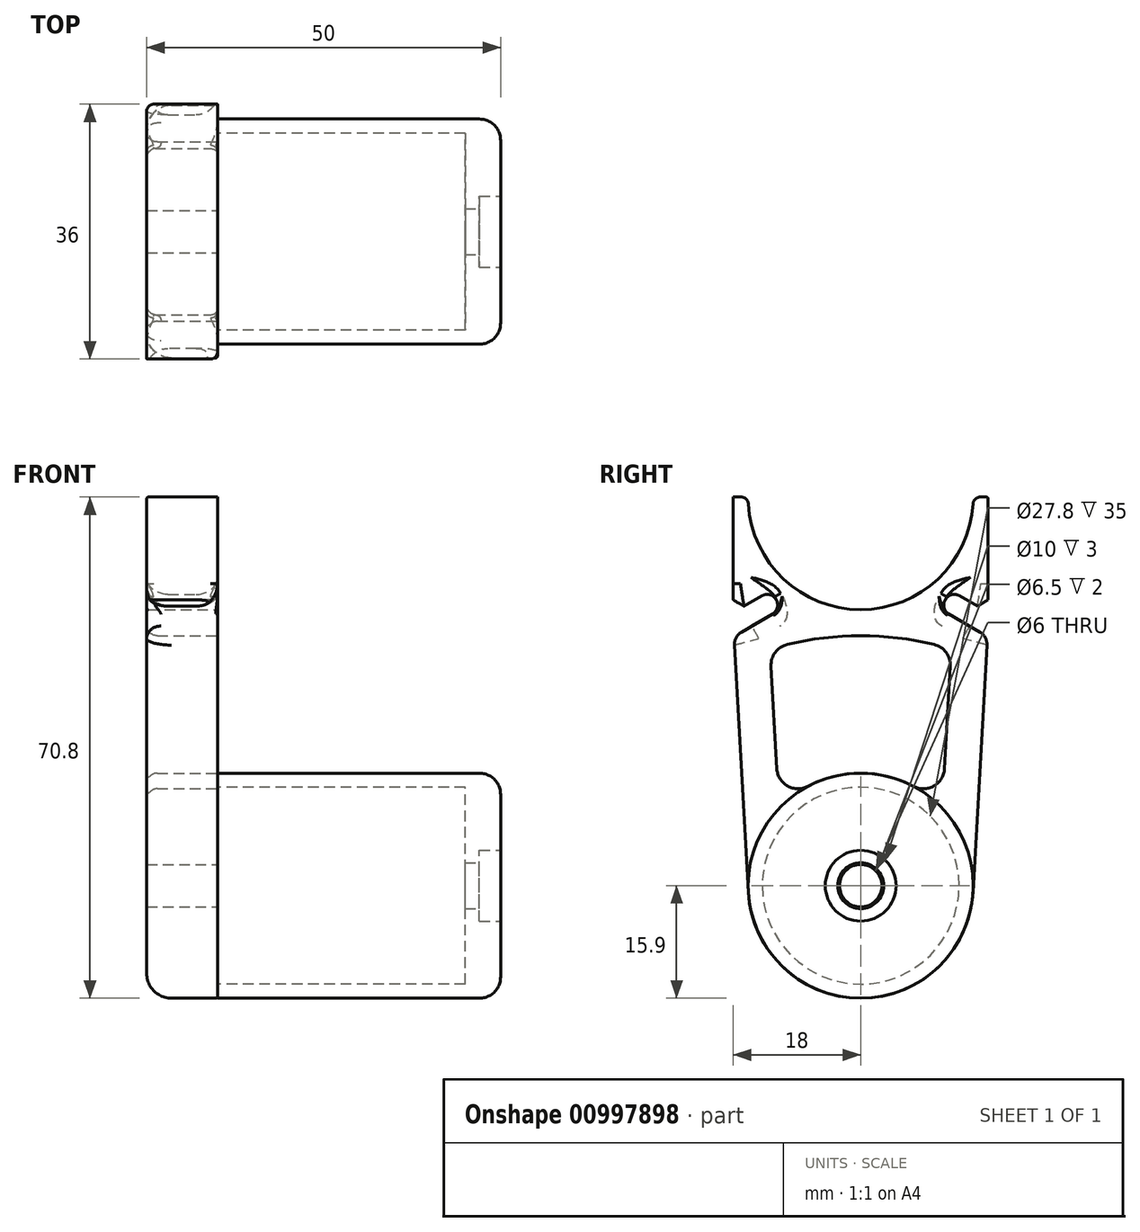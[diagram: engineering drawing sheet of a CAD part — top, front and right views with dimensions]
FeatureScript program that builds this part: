
annotation { "Feature Type Name" : "Feature", "Feature Type Description" : "" }
export const myFeature = defineFeature(function(context is Context, id is Id, definition is map)
    precondition{}
    {
        {
            var Q0;
            Q0=qCreatedBy(makeId("Right.planeOp"),FACE);
            var sketch = newSketch(context, id + "F0", { "sketchPlane" : qUnion([Q0])});
            skArc(sketch, "E0", {"start": v(-15.9, 0) * mm, "mid": v(0, -15.9) * mm, "end": v(15.9, 0) * mm});
            skArc(sketch, "E1", {"start": v(-18, 0) * mm, "mid": v(0, -18) * mm, "end": v(18, 0) * mm, "construction": true});
            skLineSegment(sketch, "E2", {"start": v(0, 0) * mm, "end": v(-18, 0) * mm});
            skLineSegment(sketch, "E3", {"start": v(0, 0) * mm, "end": v(0, -57.9) * mm, "construction": true});
            skCircle(sketch, "E4", {"center": v(0, -54.9) * mm, "radius": 15.9 * mm});
            skLineSegment(sketch, "E5", {"start": v(18, 0) * mm, "end": v(0, 0) * mm});
            skLineSegment(sketch, "E6", {"start": v(-15.93, -54.9) * mm, "end": v(15.93, -54.9) * mm});
            skCircle(sketch, "E7", {"center": v(0, -54.9) * mm, "radius": 3 * mm});
            skPoint(sketch, "E8", {"position": v(0, -18) * mm});
            skPoint(sketch, "E9", {"position": v(0, -39) * mm});
            skCircle(sketch, "E10", {"center": v(0, -54.9) * mm, "radius": 13.9 * mm});
            skLineSegment(sketch, "E11", {"start": v(15.9, 0) * mm, "end": v(15.9, -54.9) * mm, "construction": true});
            skLineSegment(sketch, "E12", {"start": v(-15.9, 0) * mm, "end": v(-15.9, -54.9) * mm, "construction": true});
            skLineSegment(sketch, "E13", {"start": v(18, 0) * mm, "end": v(18, -18) * mm});
            skLineSegment(sketch, "E14", {"start": v(-18, 0) * mm, "end": v(-18, -18) * mm});
            skLineSegment(sketch, "E15", {"start": v(18, -18) * mm, "end": v(15.87, -55.8) * mm});
            skLineSegment(sketch, "E16", {"start": v(-18, -18) * mm, "end": v(-15.87, -55.8) * mm});
            skLineSegment(sketch, "E17", {"start": v(-18, -18) * mm, "end": v(-11.94, -14.5) * mm, "construction": true});
            skCircle(sketch, "E18", {"center": v(-11.94, -14.5) * mm, "radius": 1.5 * mm});
            skLineSegment(sketch, "E19", {"start": v(-11.94, -14.5) * mm, "end": v(-12.69, -13.2) * mm, "construction": true});
            skLineSegment(sketch, "E20", {"start": v(-12.69, -13.2) * mm, "end": v(-18, -16.27) * mm});
            skLineSegment(sketch, "E21", {"start": v(-11.94, -14.5) * mm, "end": v(-11.19, -15.8) * mm, "construction": true});
            skLineSegment(sketch, "E22", {"start": v(-11.19, -15.8) * mm, "end": v(-17.9, -19.68) * mm});
            skLineSegment(sketch, "E23.MirrorCS", {"start": v(12.69, -13.2) * mm, "end": v(18, -16.27) * mm});
            skCircle(sketch, "E24.MirrorC", {"center": v(11.94, -14.5) * mm, "radius": 1.5 * mm});
            skLineSegment(sketch, "E25.MirrorCS", {"start": v(11.19, -15.8) * mm, "end": v(17.9, -19.68) * mm});
            skLineSegment(sketch, "E26", {"start": v(-12.8, -21.48) * mm, "end": v(-11.53, -43.95) * mm});
            skLineSegment(sketch, "E27", {"start": v(12.8, -21.48) * mm, "end": v(11.53, -43.95) * mm});
            skArc(sketch, "E28.trimOffspring", {"start": v(-12.8, -21.48) * mm, "mid": v(0, -25.18) * mm, "end": v(12.8, -21.48) * mm});
            skLineSegment(sketch, "E29", {"start": v(12.8, -21.48) * mm, "end": v(-12.8, -21.48) * mm, "construction": true});
            skArc(sketch, "E30", {"start": v(12.8, -21.48) * mm, "mid": v(0, -19.59) * mm, "end": v(-12.8, -21.48) * mm});
            skLineSegment(sketch, "E31", {"start": v(-17.9, -19.68) * mm, "end": v(17.9, -19.68) * mm});
            skLineSegment(sketch, "E32", {"start": v(12.69, -13.2) * mm, "end": v(11.19, -15.8) * mm});
            skLineSegment(sketch, "E33", {"start": v(-12.69, -13.2) * mm, "end": v(-11.19, -15.8) * mm});
            skSolve(sketch);
        }
        {
            var Q0;
            {var subQ0=sQuery(id+"F0.wireOp",EDGE,"hCOq8FCj-mZPl-xb8t-M9cf-22ctuRcThsnU");Q0=makeQuery(id+"F0.imprint","IMPRINT",FACE,{"disambiguationData":[TD([[makeQuery(id+"F0.imprint","IMPRINT",EDGE,{"derivedFrom":subQ0}),-1.0]])]});}
            var Q1;
            {var subQ0=sQuery(id+"F0.wireOp",EDGE,"TaPYkj7w-x2AP-gBk1-BHdD-hzMeUHBt6qgc");Q1=makeQuery(id+"F0.imprint","IMPRINT",FACE,{"disambiguationData":[TD([[makeQuery(id+"F0.imprint","IMPRINT",EDGE,{"derivedFrom":subQ0}),1.0]])]});}
            var Q2;
            {var subQ5=sQuery(id+"F0.wireOp",EDGE,"6MMxsrJf-m4Ve-tTBv-1n6J-gzjikBUi8nmd");Q2=makeQuery(id+"F0.imprint","IMPRINT",FACE,{"disambiguationData":[TD([[makeQuery(id+"F0.imprint","IMPRINT",EDGE,{"derivedFrom":subQ5}),-1.0]])]});}
            var Q3;
            {var subQ0=sQuery(id+"F0.wireOp",EDGE,"ev4YOO8p-w140-sNIP-OVyz-yG1uIH5KCiYH");Q3=makeQuery(id+"F0.imprint","IMPRINT",FACE,{"disambiguationData":[TD([[makeQuery(id+"F0.imprint","IMPRINT",EDGE,{"derivedFrom":subQ0}),1.0]])]});}
            var Q4;
            {var subQ0=sQuery(id+"F0.wireOp",EDGE,"TuPFUTSs-Mdkt-fsBn-U9RT-kbwSlqQY4cYo");Q4=makeQuery(id+"F0.imprint","IMPRINT",FACE,{"disambiguationData":[TD([[makeQuery(id+"F0.imprint","IMPRINT",EDGE,{"derivedFrom":subQ0}),-1.0]])]});}
            var Q5;
            {var subQ0=sQuery(id+"F0.wireOp",EDGE,"BNH5TMII-rD8g-z0Vy-wBGW-XPU128KKju92");Q5=makeQuery(id+"F0.imprint","IMPRINT",FACE,{"disambiguationData":[TD([[makeQuery(id+"F0.imprint","IMPRINT",EDGE,{"derivedFrom":subQ0}),-1.0]])]});}
            var Q6;
            Q6=makeQuery(id+"F0.imprint","IMPRINT",FACE,{"disambiguationData":[TD([[makeQuery(id+"F0.imprint","IMPRINT",EDGE,{"derivedFrom":sQuery(id+"F0.wireOp",EDGE,"TuPFUTSs-Mdkt-fsBn-U9RT-kbwSlqQY4cYo")}),1.0]])]});
            var Q7;
            {var subQ0=sQuery(id+"F0.wireOp",EDGE,"qgnF70fx-FksF-CE6E-BVKT-dnHn9iPgRWFa");Q7=makeQuery(id+"F0.imprint","IMPRINT",FACE,{"disambiguationData":[TD([[makeQuery(id+"F0.imprint","IMPRINT",EDGE,{"derivedFrom":subQ0}),1.0]])]});}
            var Q8;
            {var subQ1=sQuery(id+"F0.wireOp",EDGE,"E0");var subQ3=sQuery(id+"F0.wireOp",EDGE,"8emj3K5Y-vfSL-qXS8-FGDl-GD4WZCmneeYx");var subQ4=makeQuery(id+"F0.imprint","INTERSECT",VERTEX,{"derivedFrom":[subQ1,subQ3]});Q8=makeQuery(id+"F0.imprint","IMPRINT",FACE,{"disambiguationData":[TD([[makeQuery(id+"F0.imprint","IMPRINT",EDGE,{"disambiguationData":[TD([[subQ4,1.0]])],"derivedFrom":subQ3}),1.0]])]});}
            var Q9;
            {var subQ4=sQuery(id+"F0.wireOp",EDGE,"4b9Ultii-NDLb-Hdy1-wgni-m4wKdF3KNtY6");Q9=makeQuery(id+"F0.imprint","IMPRINT",FACE,{"disambiguationData":[TD([[makeQuery(id+"F0.imprint","IMPRINT",EDGE,{"derivedFrom":subQ4}),1.0]])]});}
            var Q10;
            {var subQ1=sQuery(id+"F0.wireOp",EDGE,"E0");var subQ3=sQuery(id+"F0.wireOp",EDGE,"9gYWYnP8-HUed-MIOg-rzxO-PlR66y88BDPI");var subQ4=makeQuery(id+"F0.imprint","INTERSECT",VERTEX,{"derivedFrom":[subQ1,subQ3]});Q10=makeQuery(id+"F0.imprint","IMPRINT",FACE,{"disambiguationData":[TD([[makeQuery(id+"F0.imprint","IMPRINT",EDGE,{"disambiguationData":[TD([[subQ4,1.0]])],"derivedFrom":subQ3}),-1.0]])]});}
            var Q11;
            {var subQ0=sQuery(id+"F0.wireOp",EDGE,"E12");var subQ1=sQuery(id+"F0.wireOp",EDGE,"E1");var subQ2=makeQuery(id+"F0.imprint","INTERSECT",VERTEX,{"derivedFrom":[subQ1,subQ0]});Q11=makeQuery(id+"F0.imprint","IMPRINT",FACE,{"disambiguationData":[TD([[makeQuery(id+"F0.imprint","IMPRINT",EDGE,{"disambiguationData":[TD([[subQ2,-1.0]])],"derivedFrom":subQ1}),-1.0]])]});}
            var Q12;
            {var subQ1=sQuery(id+"F0.wireOp",EDGE,"8emj3K5Y-vfSL-qXS8-FGDl-GD4WZCmneeYx");var subQ3=sQuery(id+"F0.wireOp",EDGE,"E1");var subQ4=makeQuery(id+"F0.imprint","INTERSECT",VERTEX,{"derivedFrom":[subQ3,subQ1]});Q12=makeQuery(id+"F0.imprint","IMPRINT",FACE,{"disambiguationData":[TD([[makeQuery(id+"F0.imprint","IMPRINT",EDGE,{"disambiguationData":[TD([[subQ4,-1.0]])],"derivedFrom":subQ3}),-1.0]])]});}
            var Q13;
            {var subQ0=sQuery(id+"F0.wireOp",EDGE,"9gYWYnP8-HUed-MIOg-rzxO-PlR66y88BDPI");var subQ1=sQuery(id+"F0.wireOp",EDGE,"E1");var subQ2=makeQuery(id+"F0.imprint","INTERSECT",VERTEX,{"derivedFrom":[subQ1,subQ0]});Q13=makeQuery(id+"F0.imprint","IMPRINT",FACE,{"disambiguationData":[TD([[makeQuery(id+"F0.imprint","IMPRINT",EDGE,{"disambiguationData":[TD([[subQ2,-1.0]])],"derivedFrom":subQ1}),-1.0]])]});}
            var Q14;
            Q14=makeQuery(id+"F0.imprint","IMPRINT",FACE,{"disambiguationData":[TD([[makeQuery(id+"F0.imprint","IMPRINT",EDGE,{"derivedFrom":sQuery(id+"F0.wireOp",EDGE,"6R3bmdMW-g6tU-yjxk-HsSZ-tdWfC2ykRPMh")}),-1.0]])]});
            var Q15;
            {var subQ0=sQuery(id+"F0.wireOp",EDGE,"E4");var subQ7=makeQuery(id+"F0.imprint","INTERSECT",VERTEX,{"derivedFrom":[subQ0,sQuery(id+"F0.wireOp",EDGE,"E16")]});Q15=makeQuery(id+"F0.imprint","IMPRINT",FACE,{"disambiguationData":[TD([[makeQuery(id+"F0.imprint","IMPRINT",EDGE,{"disambiguationData":[TD([[subQ7,1.0]])],"derivedFrom":subQ0}),1.0]])]});}
            var Q16;
            {var subQ8=sQuery(id+"F0.wireOp",EDGE,"E26");Q16=makeQuery(id+"F0.imprint","IMPRINT",FACE,{"disambiguationData":[TD([[makeQuery(id+"F0.imprint","IMPRINT",EDGE,{"derivedFrom":subQ8}),-1.0]])]});}
            var Q17;
            {var subQ1=sQuery(id+"F0.wireOp",EDGE,"E4");var subQ6=makeQuery(id+"F0.imprint","INTERSECT",VERTEX,{"derivedFrom":[subQ1,sQuery(id+"F0.wireOp",EDGE,"E27")]});Q17=makeQuery(id+"F0.imprint","IMPRINT",FACE,{"disambiguationData":[TD([[makeQuery(id+"F0.imprint","IMPRINT",EDGE,{"disambiguationData":[TD([[subQ6,1.0]])],"derivedFrom":subQ1}),1.0]])]});}
            var Q18;
            Q18=makeQuery(id+"F0.imprint","IMPRINT",FACE,{"disambiguationData":[TD([[makeQuery(id+"F0.imprint","IMPRINT",EDGE,{"derivedFrom":sQuery(id+"F0.wireOp",EDGE,"SB0yHOxI-lRpt-iEP2-3W7u-v9B3a5rHVDpD")}),-1.0]])]});
            var Q19;
            {var subQ4=sQuery(id+"F0.wireOp",EDGE,"E22");Q19=makeQuery(id+"F0.imprint","IMPRINT",FACE,{"disambiguationData":[TD([[makeQuery(id+"F0.imprint","IMPRINT",EDGE,{"derivedFrom":subQ4}),1.0]])]});}
            var Q20;
            {var subQ0=sQuery(id+"F0.wireOp",EDGE,"E16");var subQ1=sQuery(id+"F0.wireOp",EDGE,"E4");var subQ2=makeQuery(id+"F0.imprint","INTERSECT",VERTEX,{"derivedFrom":[subQ1,subQ0]});Q20=makeQuery(id+"F0.imprint","IMPRINT",FACE,{"disambiguationData":[TD([[makeQuery(id+"F0.imprint","IMPRINT",EDGE,{"disambiguationData":[TD([[subQ2,1.0]])],"derivedFrom":subQ1}),-1.0]])]});}
            var Q21;
            {var subQ0=sQuery(id+"F0.wireOp",EDGE,"E15");var subQ1=sQuery(id+"F0.wireOp",EDGE,"E4");var subQ2=makeQuery(id+"F0.imprint","INTERSECT",VERTEX,{"derivedFrom":[subQ1,subQ0]});Q21=makeQuery(id+"F0.imprint","IMPRINT",FACE,{"disambiguationData":[TD([[makeQuery(id+"F0.imprint","IMPRINT",EDGE,{"disambiguationData":[TD([[subQ2,-1.0]])],"derivedFrom":subQ1}),-1.0]])]});}
            var Q22;
            {var subQ0=sQuery(id+"F0.wireOp",EDGE,"E33");Q22=makeQuery(id+"F0.imprint","IMPRINT",FACE,{"disambiguationData":[TD([[makeQuery(id+"F0.imprint","IMPRINT",EDGE,{"derivedFrom":subQ0}),1.0]])]});}
            var Q23;
            {var subQ0=sQuery(id+"F0.wireOp",EDGE,"E32");Q23=makeQuery(id+"F0.imprint","IMPRINT",FACE,{"disambiguationData":[TD([[makeQuery(id+"F0.imprint","IMPRINT",EDGE,{"derivedFrom":subQ0}),-1.0]])]});}
            var Q24;
            {var subQ5=sQuery(id+"F0.wireOp",EDGE,"E27");Q24=makeQuery(id+"F0.imprint","IMPRINT",FACE,{"disambiguationData":[TD([[makeQuery(id+"F0.imprint","IMPRINT",EDGE,{"derivedFrom":subQ5}),1.0]])]});}
            var Q25;
            {var subQ0=sQuery(id+"F0.wireOp",EDGE,"E10");var subQ1=sQuery(id+"F0.wireOp",EDGE,"E6");var subQ2=makeQuery(id+"F0.imprint","INTERSECT",VERTEX,{"disambiguationData":[OD(0.0)],"derivedFrom":[subQ1,subQ0]});Q25=makeQuery(id+"F0.imprint","IMPRINT",FACE,{"disambiguationData":[TD([[makeQuery(id+"F0.imprint","IMPRINT",EDGE,{"disambiguationData":[TD([[subQ2,-1.0]])],"derivedFrom":subQ1}),-1.0]])]});}
            var Q26;
            {var subQ0=sQuery(id+"F0.wireOp",EDGE,"E10");var subQ1=sQuery(id+"F0.wireOp",EDGE,"E6");var subQ2=makeQuery(id+"F0.imprint","INTERSECT",VERTEX,{"disambiguationData":[OD(0.0)],"derivedFrom":[subQ1,subQ0]});Q26=makeQuery(id+"F0.imprint","IMPRINT",FACE,{"disambiguationData":[TD([[makeQuery(id+"F0.imprint","IMPRINT",EDGE,{"disambiguationData":[TD([[subQ2,-1.0]])],"derivedFrom":subQ1}),1.0]])]});}
            extrude(context, id + "F1", {"entities" : qUnion([Q0, Q1, Q2, Q3, Q4, Q5, Q6, Q7, Q8, Q9, Q10, Q11, Q12, Q13, Q14, Q15, Q16, Q17, Q18, Q19, Q20, Q21, Q22, Q23, Q24, Q25, Q26]), "endBound" : BoundingType.SYMMETRIC, "oppositeDirection" : true, "depth" : 10 * mm, "offsetDistance" : 25 * mm, "hasSecondDirection" : true, "secondDirectionOppositeDirection" : false, "secondDirectionDepth" : 3 * mm});
        }
        {
            var Q0;
            Q0=makeQuery(id+"F1.opExtrude","SWEPT_EDGE",EDGE,{"disambiguationData":[OSD([sQuery(id+"F0.wireOp",EDGE,"E14"),sQuery(id+"F0.wireOp",EDGE,"E20")])]});
            var Q1;
            Q1=makeQuery(id+"F1.opExtrude","SWEPT_EDGE",EDGE,{"disambiguationData":[OSD([sQuery(id+"F0.wireOp",EDGE,"E13"),sQuery(id+"F0.wireOp",EDGE,"E23.MirrorCS")])]});
            chamfer(context, id + "F2", {"entities" : qUnion([Q0, Q1]), "width" : 1 * mm, "tangentPropagation" : true});
        }
        {
            var Q0;
            Q0=makeQuery(id+"F1.opExtrude","CAP_EDGE",EDGE,{"disambiguationData":[OSD([sQuery(id+"F0.wireOp",EDGE,"E20")])],"isStart":true});
            var Q1;
            Q1=makeQuery(id+"F1.opExtrude","CAP_EDGE",EDGE,{"disambiguationData":[OSD([sQuery(id+"F0.wireOp",EDGE,"E20")])],"isStart":false});
            var Q2;
            Q2=makeQuery(id+"F1.opExtrude","CAP_EDGE",EDGE,{"disambiguationData":[OSD([sQuery(id+"F0.wireOp",EDGE,"E23.MirrorCS")])],"isStart":false});
            var Q3;
            Q3=makeQuery(id+"F1.opExtrude","CAP_EDGE",EDGE,{"disambiguationData":[OSD([sQuery(id+"F0.wireOp",EDGE,"E23.MirrorCS")])],"isStart":true});
            fillet(context, id + "F3", {"entities" : qUnion([Q0, Q1, Q2, Q3]), "tangentPropagation" : true, "radius" : 3 * mm, "defaultsChanged" : false, "vertexSettings" : [], "allowEdgeOverflow" : false});
        }
        {
            var Q0;
            Q0=makeQuery(id+"F3.opFillet","BLEND_EDGE",EDGE,{"blendedFrom":[makeQuery(id+"F1.opExtrude","CAP_EDGE",EDGE,{"disambiguationData":[OSD([sQuery(id+"F0.wireOp",EDGE,"E20")])],"isStart":true}),makeQuery(id+"F1.opExtrude","SWEPT_FACE",FACE,{"disambiguationData":[OSD([sQuery(id+"F0.wireOp",EDGE,"E14")])]})],"blendedInto":[makeQuery(id+"F1.opExtrude","SWEPT_FACE",FACE,{"disambiguationData":[OSD([sQuery(id+"F0.wireOp",EDGE,"E14")])]})]});
            var Q1;
            Q1=makeQuery(id+"F1.opExtrude","CAP_EDGE",EDGE,{"disambiguationData":[OSD([sQuery(id+"F0.wireOp",EDGE,"E13")])],"isStart":false});
            fillet(context, id + "F4", {"entities" : qUnion([Q0, Q1]), "tangentPropagation" : true, "radius" : 1 * mm, "defaultsChanged" : false, "vertexSettings" : [], "allowEdgeOverflow" : false});
        }
        {
            var Q0;
            Q0=makeQuery(id+"F1.opExtrude","SWEPT_EDGE",EDGE,{"disambiguationData":[OSD([sQuery(id+"F0.wireOp",EDGE,"E0"),sQuery(id+"F0.wireOp",EDGE,"E2")])]});
            var Q1;
            Q1=makeQuery(id+"F1.opExtrude","SWEPT_EDGE",EDGE,{"disambiguationData":[OSD([sQuery(id+"F0.wireOp",EDGE,"E0"),sQuery(id+"F0.wireOp",EDGE,"E5")])]});
            fillet(context, id + "F5", {"entities" : qUnion([Q0, Q1]), "tangentPropagation" : true, "radius" : 1 * mm, "defaultsChanged" : true, "vertexSettings" : [], "allowEdgeOverflow" : false});
        }
        {
            var Q0;
            Q0=makeQuery(id+"F1.opExtrude","CAP_EDGE",EDGE,{"disambiguationData":[OSD([sQuery(id+"F0.wireOp",EDGE,"E0")])],"isStart":false});
            fillet(context, id + "F6", {"entities" : qUnion([Q0]), "tangentPropagation" : true, "radius" : .25 * mm, "defaultsChanged" : false, "vertexSettings" : [], "allowEdgeOverflow" : false});
        }
        {
            var Q0;
            Q0=makeQuery(id+"F1.opExtrude","CAP_EDGE",EDGE,{"disambiguationData":[OSD([sQuery(id+"F0.wireOp",EDGE,"E15")])],"isStart":false});
            fillet(context, id + "F7", {"entities" : qUnion([Q0]), "tangentPropagation" : true, "radius" : 3.5 * mm, "defaultsChanged" : false, "vertexSettings" : [], "allowEdgeOverflow" : false});
        }
        {
            var Q0;
            Q0=makeQuery(id+"F1.opExtrude","SWEPT_EDGE",EDGE,{"disambiguationData":[OSD([sQuery(id+"F0.wireOp",EDGE,"E23.MirrorCS"),sQuery(id+"F0.wireOp",EDGE,"E24.MirrorC"),sQuery(id+"F0.wireOp",EDGE,"E32")])]});
            var Q1;
            Q1=makeQuery(id+"F3.opFillet","BLEND_EDGE",EDGE,{"blendedFrom":[makeQuery(id+"F1.opExtrude","CAP_EDGE",EDGE,{"disambiguationData":[OSD([sQuery(id+"F0.wireOp",EDGE,"E20")])],"isStart":false}),makeQuery(id+"F1.opExtrude","SWEPT_FACE",FACE,{"disambiguationData":[OSD([sQuery(id+"F0.wireOp",EDGE,"E33")])]})],"blendedInto":[makeQuery(id+"F1.opExtrude","SWEPT_FACE",FACE,{"disambiguationData":[OSD([sQuery(id+"F0.wireOp",EDGE,"E33")])]})]});
            fillet(context, id + "F8", {"entities" : qUnion([Q0, Q1]), "tangentPropagation" : true, "radius" : 1.5 * mm, "defaultsChanged" : true, "vertexSettings" : [], "allowEdgeOverflow" : false});
        }
        {
            var Q0;
            Q0=makeQuery(id+"F1.opExtrude","CAP_EDGE",EDGE,{"disambiguationData":[OSD([sQuery(id+"F0.wireOp",EDGE,"E32")])],"isStart":false});
            var Q1;
            Q1=makeQuery(id+"F1.opExtrude","CAP_EDGE",EDGE,{"disambiguationData":[OSD([sQuery(id+"F0.wireOp",EDGE,"E32")])],"isStart":true});
            var Q2;
            Q2=makeQuery(id+"F1.opExtrude","CAP_EDGE",EDGE,{"disambiguationData":[OSD([sQuery(id+"F0.wireOp",EDGE,"E33")])],"isStart":false});
            var Q3;
            Q3=makeQuery(id+"F1.opExtrude","CAP_EDGE",EDGE,{"disambiguationData":[OSD([sQuery(id+"F0.wireOp",EDGE,"E33")])],"isStart":true});
            fillet(context, id + "F9", {"entities" : qUnion([Q0, Q1, Q2, Q3]), "tangentPropagation" : true, "radius" : 1 * mm, "defaultsChanged" : false, "vertexSettings" : [], "allowEdgeOverflow" : false});
        }
        {
            var Q0;
            Q0=makeQuery(id+"F1.opExtrude","SWEPT_EDGE",EDGE,{"disambiguationData":[OSD([sQuery(id+"F0.wireOp",EDGE,"E24.MirrorC"),sQuery(id+"F0.wireOp",EDGE,"E25.MirrorCS"),sQuery(id+"F0.wireOp",EDGE,"E32")])]});
            var Q1;
            {var subQ0=sQuery(id+"F0.wireOp",EDGE,"E2");var subQ1=sQuery(id+"F0.wireOp",EDGE,"E0");var subQ2=makeQuery(id+"F1.opExtrude","CAP_FACE",FACE,{"disambiguationData":[OSD([subQ1,subQ0,sQuery(id+"F0.wireOp",EDGE,"E4"),sQuery(id+"F0.wireOp",EDGE,"E5"),sQuery(id+"F0.wireOp",EDGE,"E7"),sQuery(id+"F0.wireOp",EDGE,"SB0yHOxI-lRpt-iEP2-3W7u-v9B3a5rHVDpD"),sQuery(id+"F0.wireOp",EDGE,"LhZdfopr-r1uI-wH8t-D8PB-L3U7t8i66CS0"),sQuery(id+"F0.wireOp",EDGE,"cogAvgOB-P8PS-PaiP-QbT0-jrrfWqRzv5wB"),sQuery(id+"F0.wireOp",EDGE,"6R3bmdMW-g6tU-yjxk-HsSZ-tdWfC2ykRPMh"),sQuery(id+"F0.wireOp",EDGE,"E13"),sQuery(id+"F0.wireOp",EDGE,"E14"),sQuery(id+"F0.wireOp",EDGE,"E15"),sQuery(id+"F0.wireOp",EDGE,"E16"),sQuery(id+"F0.wireOp",EDGE,"E20"),sQuery(id+"F0.wireOp",EDGE,"E22"),sQuery(id+"F0.wireOp",EDGE,"E23.MirrorCS"),sQuery(id+"F0.wireOp",EDGE,"E25.MirrorCS"),sQuery(id+"F0.wireOp",EDGE,"E26"),sQuery(id+"F0.wireOp",EDGE,"E27"),sQuery(id+"F0.wireOp",EDGE,"E30"),sQuery(id+"F0.wireOp",EDGE,"E32"),sQuery(id+"F0.wireOp",EDGE,"E33")])],"isStart":false});Q1=makeQuery(id+"F6.opFillet","BLEND_EDGE",EDGE,{"blendedFrom":[makeQuery(id+"F5.opFillet","BLEND_EDGE",EDGE,{"blendedFrom":[makeQuery(id+"F1.opExtrude","SWEPT_EDGE",EDGE,{"disambiguationData":[OSD([subQ1,subQ0])]}),subQ2],"blendedInto":[subQ2]}),subQ2],"blendedInto":[subQ2]});}
            var Q2;
            {var subQ0=sQuery(id+"F0.wireOp",EDGE,"E2");Q2=makeQuery(id+"F6.opFillet","BLEND_EDGE",EDGE,{"blendedFrom":[makeQuery(id+"F4.opFillet","BLEND_EDGE",EDGE,{"disambiguationData":[OD(1.0)],"blendedFrom":[makeQuery(id+"F1.opExtrude","CAP_EDGE",EDGE,{"disambiguationData":[OSD([sQuery(id+"F0.wireOp",EDGE,"E14")])],"isStart":true}),makeQuery(id+"F1.opExtrude","SWEPT_FACE",FACE,{"disambiguationData":[OSD([subQ0])]})],"blendedInto":[makeQuery(id+"F1.opExtrude","SWEPT_FACE",FACE,{"disambiguationData":[OSD([subQ0])]})]}),makeQuery(id+"F1.opExtrude","CAP_EDGE",EDGE,{"disambiguationData":[OSD([subQ0])],"isStart":false})],"blendedInto":[]});}
            var Q3;
            {var subQ0=sQuery(id+"F0.wireOp",EDGE,"E14");Q3=makeQuery(id+"F6.opFillet","BLEND_EDGE",EDGE,{"blendedFrom":[makeQuery(id+"F4.opFillet","BLEND_EDGE",EDGE,{"disambiguationData":[OD(1.0)],"blendedFrom":[makeQuery(id+"F1.opExtrude","CAP_EDGE",EDGE,{"disambiguationData":[OSD([subQ0])],"isStart":true}),makeQuery(id+"F1.opExtrude","SWEPT_FACE",FACE,{"disambiguationData":[OSD([sQuery(id+"F0.wireOp",EDGE,"E2")])]})],"blendedInto":[makeQuery(id+"F1.opExtrude","SWEPT_FACE",FACE,{"disambiguationData":[OSD([sQuery(id+"F0.wireOp",EDGE,"E2")])]})]}),makeQuery(id+"F4.opFillet","BLEND_FACE",FACE,{"disambiguationData":[OSD([subQ0]),OD(1.0)]})],"blendedInto":[makeQuery(id+"F4.opFillet","BLEND_FACE",FACE,{"disambiguationData":[OSD([subQ0]),OD(1.0)]})]});}
            var Q4;
            {var subQ0=sQuery(id+"F0.wireOp",EDGE,"E2");var subQ1=sQuery(id+"F0.wireOp",EDGE,"E0");Q4=makeQuery(id+"F6.opFillet","BLEND_EDGE",EDGE,{"blendedFrom":[makeQuery(id+"F5.opFillet","BLEND_EDGE",EDGE,{"blendedFrom":[makeQuery(id+"F1.opExtrude","SWEPT_EDGE",EDGE,{"disambiguationData":[OSD([subQ1,subQ0])]}),makeQuery(id+"F1.opExtrude","CAP_FACE",FACE,{"disambiguationData":[OSD([subQ1,subQ0,sQuery(id+"F0.wireOp",EDGE,"E4"),sQuery(id+"F0.wireOp",EDGE,"E5"),sQuery(id+"F0.wireOp",EDGE,"E7"),sQuery(id+"F0.wireOp",EDGE,"SB0yHOxI-lRpt-iEP2-3W7u-v9B3a5rHVDpD"),sQuery(id+"F0.wireOp",EDGE,"LhZdfopr-r1uI-wH8t-D8PB-L3U7t8i66CS0"),sQuery(id+"F0.wireOp",EDGE,"cogAvgOB-P8PS-PaiP-QbT0-jrrfWqRzv5wB"),sQuery(id+"F0.wireOp",EDGE,"6R3bmdMW-g6tU-yjxk-HsSZ-tdWfC2ykRPMh"),sQuery(id+"F0.wireOp",EDGE,"E13"),sQuery(id+"F0.wireOp",EDGE,"E14"),sQuery(id+"F0.wireOp",EDGE,"E15"),sQuery(id+"F0.wireOp",EDGE,"E16"),sQuery(id+"F0.wireOp",EDGE,"E20"),sQuery(id+"F0.wireOp",EDGE,"E22"),sQuery(id+"F0.wireOp",EDGE,"E23.MirrorCS"),sQuery(id+"F0.wireOp",EDGE,"E25.MirrorCS"),sQuery(id+"F0.wireOp",EDGE,"E26"),sQuery(id+"F0.wireOp",EDGE,"E27"),sQuery(id+"F0.wireOp",EDGE,"E30"),sQuery(id+"F0.wireOp",EDGE,"E32"),sQuery(id+"F0.wireOp",EDGE,"E33")])],"isStart":false})],"blendedInto":[makeQuery(id+"F1.opExtrude","CAP_FACE",FACE,{"disambiguationData":[OSD([subQ1,subQ0,sQuery(id+"F0.wireOp",EDGE,"E4"),sQuery(id+"F0.wireOp",EDGE,"E5"),sQuery(id+"F0.wireOp",EDGE,"E7"),sQuery(id+"F0.wireOp",EDGE,"SB0yHOxI-lRpt-iEP2-3W7u-v9B3a5rHVDpD"),sQuery(id+"F0.wireOp",EDGE,"LhZdfopr-r1uI-wH8t-D8PB-L3U7t8i66CS0"),sQuery(id+"F0.wireOp",EDGE,"cogAvgOB-P8PS-PaiP-QbT0-jrrfWqRzv5wB"),sQuery(id+"F0.wireOp",EDGE,"6R3bmdMW-g6tU-yjxk-HsSZ-tdWfC2ykRPMh"),sQuery(id+"F0.wireOp",EDGE,"E13"),sQuery(id+"F0.wireOp",EDGE,"E14"),sQuery(id+"F0.wireOp",EDGE,"E15"),sQuery(id+"F0.wireOp",EDGE,"E16"),sQuery(id+"F0.wireOp",EDGE,"E20"),sQuery(id+"F0.wireOp",EDGE,"E22"),sQuery(id+"F0.wireOp",EDGE,"E23.MirrorCS"),sQuery(id+"F0.wireOp",EDGE,"E25.MirrorCS"),sQuery(id+"F0.wireOp",EDGE,"E26"),sQuery(id+"F0.wireOp",EDGE,"E27"),sQuery(id+"F0.wireOp",EDGE,"E30"),sQuery(id+"F0.wireOp",EDGE,"E32"),sQuery(id+"F0.wireOp",EDGE,"E33")])],"isStart":false})]}),makeQuery(id+"F1.opExtrude","CAP_EDGE",EDGE,{"disambiguationData":[OSD([subQ0])],"isStart":false})],"blendedInto":[]});}
            var Q5;
            {var subQ0=sQuery(id+"F0.wireOp",EDGE,"E2");Q5=makeQuery(id+"F5.opFillet","BLEND_EDGE",EDGE,{"blendedFrom":[makeQuery(id+"F1.opExtrude","SWEPT_EDGE",EDGE,{"disambiguationData":[OSD([sQuery(id+"F0.wireOp",EDGE,"E0"),subQ0])]}),makeQuery(id+"F1.opExtrude","SWEPT_FACE",FACE,{"disambiguationData":[OSD([subQ0])]})],"blendedInto":[makeQuery(id+"F1.opExtrude","SWEPT_FACE",FACE,{"disambiguationData":[OSD([subQ0])]})]});}
            var Q6;
            {var subQ0=makeQuery(id+"F1.opExtrude","SWEPT_FACE",FACE,{"disambiguationData":[OSD([sQuery(id+"F0.wireOp",EDGE,"E2")])]});Q6=makeQuery(id+"F6.opFillet","BLEND_EDGE",EDGE,{"blendedFrom":[makeQuery(id+"F4.opFillet","BLEND_EDGE",EDGE,{"disambiguationData":[OD(1.0)],"blendedFrom":[makeQuery(id+"F1.opExtrude","CAP_EDGE",EDGE,{"disambiguationData":[OSD([sQuery(id+"F0.wireOp",EDGE,"E14")])],"isStart":true}),subQ0],"blendedInto":[subQ0]}),subQ0],"blendedInto":[subQ0]});}
            var Q7;
            {var subQ0=sQuery(id+"F0.wireOp",EDGE,"E2");var subQ1=sQuery(id+"F0.wireOp",EDGE,"E0");Q7=makeQuery(id+"F6.opFillet","BLEND_EDGE",EDGE,{"blendedFrom":[makeQuery(id+"F5.opFillet","BLEND_EDGE",EDGE,{"blendedFrom":[makeQuery(id+"F1.opExtrude","SWEPT_EDGE",EDGE,{"disambiguationData":[OSD([subQ1,subQ0])]}),makeQuery(id+"F1.opExtrude","CAP_FACE",FACE,{"disambiguationData":[OSD([subQ1,subQ0,sQuery(id+"F0.wireOp",EDGE,"E4"),sQuery(id+"F0.wireOp",EDGE,"E5"),sQuery(id+"F0.wireOp",EDGE,"E7"),sQuery(id+"F0.wireOp",EDGE,"SB0yHOxI-lRpt-iEP2-3W7u-v9B3a5rHVDpD"),sQuery(id+"F0.wireOp",EDGE,"LhZdfopr-r1uI-wH8t-D8PB-L3U7t8i66CS0"),sQuery(id+"F0.wireOp",EDGE,"cogAvgOB-P8PS-PaiP-QbT0-jrrfWqRzv5wB"),sQuery(id+"F0.wireOp",EDGE,"6R3bmdMW-g6tU-yjxk-HsSZ-tdWfC2ykRPMh"),sQuery(id+"F0.wireOp",EDGE,"E13"),sQuery(id+"F0.wireOp",EDGE,"E14"),sQuery(id+"F0.wireOp",EDGE,"E15"),sQuery(id+"F0.wireOp",EDGE,"E16"),sQuery(id+"F0.wireOp",EDGE,"E20"),sQuery(id+"F0.wireOp",EDGE,"E22"),sQuery(id+"F0.wireOp",EDGE,"E23.MirrorCS"),sQuery(id+"F0.wireOp",EDGE,"E25.MirrorCS"),sQuery(id+"F0.wireOp",EDGE,"E26"),sQuery(id+"F0.wireOp",EDGE,"E27"),sQuery(id+"F0.wireOp",EDGE,"E30"),sQuery(id+"F0.wireOp",EDGE,"E32"),sQuery(id+"F0.wireOp",EDGE,"E33")])],"isStart":false})],"blendedInto":[makeQuery(id+"F1.opExtrude","CAP_FACE",FACE,{"disambiguationData":[OSD([subQ1,subQ0,sQuery(id+"F0.wireOp",EDGE,"E4"),sQuery(id+"F0.wireOp",EDGE,"E5"),sQuery(id+"F0.wireOp",EDGE,"E7"),sQuery(id+"F0.wireOp",EDGE,"SB0yHOxI-lRpt-iEP2-3W7u-v9B3a5rHVDpD"),sQuery(id+"F0.wireOp",EDGE,"LhZdfopr-r1uI-wH8t-D8PB-L3U7t8i66CS0"),sQuery(id+"F0.wireOp",EDGE,"cogAvgOB-P8PS-PaiP-QbT0-jrrfWqRzv5wB"),sQuery(id+"F0.wireOp",EDGE,"6R3bmdMW-g6tU-yjxk-HsSZ-tdWfC2ykRPMh"),sQuery(id+"F0.wireOp",EDGE,"E13"),sQuery(id+"F0.wireOp",EDGE,"E14"),sQuery(id+"F0.wireOp",EDGE,"E15"),sQuery(id+"F0.wireOp",EDGE,"E16"),sQuery(id+"F0.wireOp",EDGE,"E20"),sQuery(id+"F0.wireOp",EDGE,"E22"),sQuery(id+"F0.wireOp",EDGE,"E23.MirrorCS"),sQuery(id+"F0.wireOp",EDGE,"E25.MirrorCS"),sQuery(id+"F0.wireOp",EDGE,"E26"),sQuery(id+"F0.wireOp",EDGE,"E27"),sQuery(id+"F0.wireOp",EDGE,"E30"),sQuery(id+"F0.wireOp",EDGE,"E32"),sQuery(id+"F0.wireOp",EDGE,"E33")])],"isStart":false})]}),makeQuery(id+"F5.opFillet","BLEND_FACE",FACE,{"disambiguationData":[OSD([subQ1,subQ0])]})],"blendedInto":[makeQuery(id+"F5.opFillet","BLEND_FACE",FACE,{"disambiguationData":[OSD([subQ1,subQ0])]})]});}
            var Q8;
            {var subQ0=sQuery(id+"F0.wireOp",EDGE,"E2");Q8=makeQuery(id+"F6.opFillet","BLEND_EDGE",EDGE,{"blendedFrom":[makeQuery(id+"F1.opExtrude","CAP_EDGE",EDGE,{"disambiguationData":[OSD([subQ0])],"isStart":false}),makeQuery(id+"F1.opExtrude","CAP_FACE",FACE,{"disambiguationData":[OSD([sQuery(id+"F0.wireOp",EDGE,"E0"),subQ0,sQuery(id+"F0.wireOp",EDGE,"E4"),sQuery(id+"F0.wireOp",EDGE,"E5"),sQuery(id+"F0.wireOp",EDGE,"E7"),sQuery(id+"F0.wireOp",EDGE,"SB0yHOxI-lRpt-iEP2-3W7u-v9B3a5rHVDpD"),sQuery(id+"F0.wireOp",EDGE,"LhZdfopr-r1uI-wH8t-D8PB-L3U7t8i66CS0"),sQuery(id+"F0.wireOp",EDGE,"cogAvgOB-P8PS-PaiP-QbT0-jrrfWqRzv5wB"),sQuery(id+"F0.wireOp",EDGE,"6R3bmdMW-g6tU-yjxk-HsSZ-tdWfC2ykRPMh"),sQuery(id+"F0.wireOp",EDGE,"E13"),sQuery(id+"F0.wireOp",EDGE,"E14"),sQuery(id+"F0.wireOp",EDGE,"E15"),sQuery(id+"F0.wireOp",EDGE,"E16"),sQuery(id+"F0.wireOp",EDGE,"E20"),sQuery(id+"F0.wireOp",EDGE,"E22"),sQuery(id+"F0.wireOp",EDGE,"E23.MirrorCS"),sQuery(id+"F0.wireOp",EDGE,"E25.MirrorCS"),sQuery(id+"F0.wireOp",EDGE,"E26"),sQuery(id+"F0.wireOp",EDGE,"E27"),sQuery(id+"F0.wireOp",EDGE,"E30"),sQuery(id+"F0.wireOp",EDGE,"E32"),sQuery(id+"F0.wireOp",EDGE,"E33")])],"isStart":false})],"blendedInto":[makeQuery(id+"F1.opExtrude","CAP_FACE",FACE,{"disambiguationData":[OSD([sQuery(id+"F0.wireOp",EDGE,"E0"),subQ0,sQuery(id+"F0.wireOp",EDGE,"E4"),sQuery(id+"F0.wireOp",EDGE,"E5"),sQuery(id+"F0.wireOp",EDGE,"E7"),sQuery(id+"F0.wireOp",EDGE,"SB0yHOxI-lRpt-iEP2-3W7u-v9B3a5rHVDpD"),sQuery(id+"F0.wireOp",EDGE,"LhZdfopr-r1uI-wH8t-D8PB-L3U7t8i66CS0"),sQuery(id+"F0.wireOp",EDGE,"cogAvgOB-P8PS-PaiP-QbT0-jrrfWqRzv5wB"),sQuery(id+"F0.wireOp",EDGE,"6R3bmdMW-g6tU-yjxk-HsSZ-tdWfC2ykRPMh"),sQuery(id+"F0.wireOp",EDGE,"E13"),sQuery(id+"F0.wireOp",EDGE,"E14"),sQuery(id+"F0.wireOp",EDGE,"E15"),sQuery(id+"F0.wireOp",EDGE,"E16"),sQuery(id+"F0.wireOp",EDGE,"E20"),sQuery(id+"F0.wireOp",EDGE,"E22"),sQuery(id+"F0.wireOp",EDGE,"E23.MirrorCS"),sQuery(id+"F0.wireOp",EDGE,"E25.MirrorCS"),sQuery(id+"F0.wireOp",EDGE,"E26"),sQuery(id+"F0.wireOp",EDGE,"E27"),sQuery(id+"F0.wireOp",EDGE,"E30"),sQuery(id+"F0.wireOp",EDGE,"E32"),sQuery(id+"F0.wireOp",EDGE,"E33")])],"isStart":false})]});}
            var Q9;
            {var subQ0=sQuery(id+"F0.wireOp",EDGE,"E14");Q9=makeQuery(id+"F4.opFillet","BLEND_EDGE",EDGE,{"blendedFrom":[makeQuery(id+"F1.opExtrude","CAP_EDGE",EDGE,{"disambiguationData":[OSD([subQ0])],"isStart":true}),makeQuery(id+"F1.opExtrude","CAP_FACE",FACE,{"disambiguationData":[OSD([sQuery(id+"F0.wireOp",EDGE,"E0"),sQuery(id+"F0.wireOp",EDGE,"E2"),sQuery(id+"F0.wireOp",EDGE,"E4"),sQuery(id+"F0.wireOp",EDGE,"E5"),sQuery(id+"F0.wireOp",EDGE,"E7"),sQuery(id+"F0.wireOp",EDGE,"SB0yHOxI-lRpt-iEP2-3W7u-v9B3a5rHVDpD"),sQuery(id+"F0.wireOp",EDGE,"LhZdfopr-r1uI-wH8t-D8PB-L3U7t8i66CS0"),sQuery(id+"F0.wireOp",EDGE,"cogAvgOB-P8PS-PaiP-QbT0-jrrfWqRzv5wB"),sQuery(id+"F0.wireOp",EDGE,"6R3bmdMW-g6tU-yjxk-HsSZ-tdWfC2ykRPMh"),sQuery(id+"F0.wireOp",EDGE,"E13"),subQ0,sQuery(id+"F0.wireOp",EDGE,"E15"),sQuery(id+"F0.wireOp",EDGE,"E16"),sQuery(id+"F0.wireOp",EDGE,"E20"),sQuery(id+"F0.wireOp",EDGE,"E22"),sQuery(id+"F0.wireOp",EDGE,"E23.MirrorCS"),sQuery(id+"F0.wireOp",EDGE,"E25.MirrorCS"),sQuery(id+"F0.wireOp",EDGE,"E26"),sQuery(id+"F0.wireOp",EDGE,"E27"),sQuery(id+"F0.wireOp",EDGE,"E30"),sQuery(id+"F0.wireOp",EDGE,"E32"),sQuery(id+"F0.wireOp",EDGE,"E33")])],"isStart":false})],"blendedInto":[makeQuery(id+"F1.opExtrude","CAP_FACE",FACE,{"disambiguationData":[OSD([sQuery(id+"F0.wireOp",EDGE,"E0"),sQuery(id+"F0.wireOp",EDGE,"E2"),sQuery(id+"F0.wireOp",EDGE,"E4"),sQuery(id+"F0.wireOp",EDGE,"E5"),sQuery(id+"F0.wireOp",EDGE,"E7"),sQuery(id+"F0.wireOp",EDGE,"SB0yHOxI-lRpt-iEP2-3W7u-v9B3a5rHVDpD"),sQuery(id+"F0.wireOp",EDGE,"LhZdfopr-r1uI-wH8t-D8PB-L3U7t8i66CS0"),sQuery(id+"F0.wireOp",EDGE,"cogAvgOB-P8PS-PaiP-QbT0-jrrfWqRzv5wB"),sQuery(id+"F0.wireOp",EDGE,"6R3bmdMW-g6tU-yjxk-HsSZ-tdWfC2ykRPMh"),sQuery(id+"F0.wireOp",EDGE,"E13"),subQ0,sQuery(id+"F0.wireOp",EDGE,"E15"),sQuery(id+"F0.wireOp",EDGE,"E16"),sQuery(id+"F0.wireOp",EDGE,"E20"),sQuery(id+"F0.wireOp",EDGE,"E22"),sQuery(id+"F0.wireOp",EDGE,"E23.MirrorCS"),sQuery(id+"F0.wireOp",EDGE,"E25.MirrorCS"),sQuery(id+"F0.wireOp",EDGE,"E26"),sQuery(id+"F0.wireOp",EDGE,"E27"),sQuery(id+"F0.wireOp",EDGE,"E30"),sQuery(id+"F0.wireOp",EDGE,"E32"),sQuery(id+"F0.wireOp",EDGE,"E33")])],"isStart":false})]});}
            var Q10;
            {var subQ0=sQuery(id+"F0.wireOp",EDGE,"E0");Q10=makeQuery(id+"F5.opFillet","BLEND_EDGE",EDGE,{"blendedFrom":[makeQuery(id+"F1.opExtrude","SWEPT_EDGE",EDGE,{"disambiguationData":[OSD([subQ0,sQuery(id+"F0.wireOp",EDGE,"E2")])]}),makeQuery(id+"F1.opExtrude","SWEPT_FACE",FACE,{"disambiguationData":[OSD([subQ0])]})],"blendedInto":[makeQuery(id+"F1.opExtrude","SWEPT_FACE",FACE,{"disambiguationData":[OSD([subQ0])]})]});}
            var Q11;
            {var subQ0=sQuery(id+"F0.wireOp",EDGE,"E2");Q11=makeQuery(id+"F6.opFillet","BLEND_EDGE",EDGE,{"blendedFrom":[makeQuery(id+"F1.opExtrude","CAP_EDGE",EDGE,{"disambiguationData":[OSD([subQ0])],"isStart":false}),makeQuery(id+"F1.opExtrude","SWEPT_FACE",FACE,{"disambiguationData":[OSD([subQ0])]})],"blendedInto":[makeQuery(id+"F1.opExtrude","SWEPT_FACE",FACE,{"disambiguationData":[OSD([subQ0])]})]});}
            var Q12;
            {var subQ0=sQuery(id+"F0.wireOp",EDGE,"E0");Q12=makeQuery(id+"F6.opFillet","BLEND_EDGE",EDGE,{"blendedFrom":[makeQuery(id+"F1.opExtrude","CAP_EDGE",EDGE,{"disambiguationData":[OSD([subQ0])],"isStart":false}),makeQuery(id+"F1.opExtrude","SWEPT_FACE",FACE,{"disambiguationData":[OSD([subQ0])]})],"blendedInto":[makeQuery(id+"F1.opExtrude","SWEPT_FACE",FACE,{"disambiguationData":[OSD([subQ0])]})]});}
            var Q13;
            {var subQ0=sQuery(id+"F0.wireOp",EDGE,"E0");var subQ1=sQuery(id+"F0.wireOp",EDGE,"E2");Q13=makeQuery(id+"F6.opFillet","BLEND_EDGE",EDGE,{"blendedFrom":[makeQuery(id+"F5.opFillet","BLEND_EDGE",EDGE,{"blendedFrom":[makeQuery(id+"F1.opExtrude","SWEPT_EDGE",EDGE,{"disambiguationData":[OSD([subQ0,subQ1])]}),makeQuery(id+"F1.opExtrude","CAP_FACE",FACE,{"disambiguationData":[OSD([subQ0,subQ1,sQuery(id+"F0.wireOp",EDGE,"E4"),sQuery(id+"F0.wireOp",EDGE,"E5"),sQuery(id+"F0.wireOp",EDGE,"E7"),sQuery(id+"F0.wireOp",EDGE,"SB0yHOxI-lRpt-iEP2-3W7u-v9B3a5rHVDpD"),sQuery(id+"F0.wireOp",EDGE,"LhZdfopr-r1uI-wH8t-D8PB-L3U7t8i66CS0"),sQuery(id+"F0.wireOp",EDGE,"cogAvgOB-P8PS-PaiP-QbT0-jrrfWqRzv5wB"),sQuery(id+"F0.wireOp",EDGE,"6R3bmdMW-g6tU-yjxk-HsSZ-tdWfC2ykRPMh"),sQuery(id+"F0.wireOp",EDGE,"E13"),sQuery(id+"F0.wireOp",EDGE,"E14"),sQuery(id+"F0.wireOp",EDGE,"E15"),sQuery(id+"F0.wireOp",EDGE,"E16"),sQuery(id+"F0.wireOp",EDGE,"E20"),sQuery(id+"F0.wireOp",EDGE,"E22"),sQuery(id+"F0.wireOp",EDGE,"E23.MirrorCS"),sQuery(id+"F0.wireOp",EDGE,"E25.MirrorCS"),sQuery(id+"F0.wireOp",EDGE,"E26"),sQuery(id+"F0.wireOp",EDGE,"E27"),sQuery(id+"F0.wireOp",EDGE,"E30"),sQuery(id+"F0.wireOp",EDGE,"E32"),sQuery(id+"F0.wireOp",EDGE,"E33")])],"isStart":false})],"blendedInto":[makeQuery(id+"F1.opExtrude","CAP_FACE",FACE,{"disambiguationData":[OSD([subQ0,subQ1,sQuery(id+"F0.wireOp",EDGE,"E4"),sQuery(id+"F0.wireOp",EDGE,"E5"),sQuery(id+"F0.wireOp",EDGE,"E7"),sQuery(id+"F0.wireOp",EDGE,"SB0yHOxI-lRpt-iEP2-3W7u-v9B3a5rHVDpD"),sQuery(id+"F0.wireOp",EDGE,"LhZdfopr-r1uI-wH8t-D8PB-L3U7t8i66CS0"),sQuery(id+"F0.wireOp",EDGE,"cogAvgOB-P8PS-PaiP-QbT0-jrrfWqRzv5wB"),sQuery(id+"F0.wireOp",EDGE,"6R3bmdMW-g6tU-yjxk-HsSZ-tdWfC2ykRPMh"),sQuery(id+"F0.wireOp",EDGE,"E13"),sQuery(id+"F0.wireOp",EDGE,"E14"),sQuery(id+"F0.wireOp",EDGE,"E15"),sQuery(id+"F0.wireOp",EDGE,"E16"),sQuery(id+"F0.wireOp",EDGE,"E20"),sQuery(id+"F0.wireOp",EDGE,"E22"),sQuery(id+"F0.wireOp",EDGE,"E23.MirrorCS"),sQuery(id+"F0.wireOp",EDGE,"E25.MirrorCS"),sQuery(id+"F0.wireOp",EDGE,"E26"),sQuery(id+"F0.wireOp",EDGE,"E27"),sQuery(id+"F0.wireOp",EDGE,"E30"),sQuery(id+"F0.wireOp",EDGE,"E32"),sQuery(id+"F0.wireOp",EDGE,"E33")])],"isStart":false})]}),makeQuery(id+"F1.opExtrude","CAP_EDGE",EDGE,{"disambiguationData":[OSD([subQ0])],"isStart":false})],"blendedInto":[]});}
            var Q14;
            {var subQ0=sQuery(id+"F0.wireOp",EDGE,"E0");Q14=makeQuery(id+"F6.opFillet","BLEND_EDGE",EDGE,{"blendedFrom":[makeQuery(id+"F1.opExtrude","CAP_EDGE",EDGE,{"disambiguationData":[OSD([subQ0])],"isStart":false}),makeQuery(id+"F1.opExtrude","CAP_FACE",FACE,{"disambiguationData":[OSD([subQ0,sQuery(id+"F0.wireOp",EDGE,"E2"),sQuery(id+"F0.wireOp",EDGE,"E4"),sQuery(id+"F0.wireOp",EDGE,"E5"),sQuery(id+"F0.wireOp",EDGE,"E7"),sQuery(id+"F0.wireOp",EDGE,"SB0yHOxI-lRpt-iEP2-3W7u-v9B3a5rHVDpD"),sQuery(id+"F0.wireOp",EDGE,"LhZdfopr-r1uI-wH8t-D8PB-L3U7t8i66CS0"),sQuery(id+"F0.wireOp",EDGE,"cogAvgOB-P8PS-PaiP-QbT0-jrrfWqRzv5wB"),sQuery(id+"F0.wireOp",EDGE,"6R3bmdMW-g6tU-yjxk-HsSZ-tdWfC2ykRPMh"),sQuery(id+"F0.wireOp",EDGE,"E13"),sQuery(id+"F0.wireOp",EDGE,"E14"),sQuery(id+"F0.wireOp",EDGE,"E15"),sQuery(id+"F0.wireOp",EDGE,"E16"),sQuery(id+"F0.wireOp",EDGE,"E20"),sQuery(id+"F0.wireOp",EDGE,"E22"),sQuery(id+"F0.wireOp",EDGE,"E23.MirrorCS"),sQuery(id+"F0.wireOp",EDGE,"E25.MirrorCS"),sQuery(id+"F0.wireOp",EDGE,"E26"),sQuery(id+"F0.wireOp",EDGE,"E27"),sQuery(id+"F0.wireOp",EDGE,"E30"),sQuery(id+"F0.wireOp",EDGE,"E32"),sQuery(id+"F0.wireOp",EDGE,"E33")])],"isStart":false})],"blendedInto":[makeQuery(id+"F1.opExtrude","CAP_FACE",FACE,{"disambiguationData":[OSD([subQ0,sQuery(id+"F0.wireOp",EDGE,"E2"),sQuery(id+"F0.wireOp",EDGE,"E4"),sQuery(id+"F0.wireOp",EDGE,"E5"),sQuery(id+"F0.wireOp",EDGE,"E7"),sQuery(id+"F0.wireOp",EDGE,"SB0yHOxI-lRpt-iEP2-3W7u-v9B3a5rHVDpD"),sQuery(id+"F0.wireOp",EDGE,"LhZdfopr-r1uI-wH8t-D8PB-L3U7t8i66CS0"),sQuery(id+"F0.wireOp",EDGE,"cogAvgOB-P8PS-PaiP-QbT0-jrrfWqRzv5wB"),sQuery(id+"F0.wireOp",EDGE,"6R3bmdMW-g6tU-yjxk-HsSZ-tdWfC2ykRPMh"),sQuery(id+"F0.wireOp",EDGE,"E13"),sQuery(id+"F0.wireOp",EDGE,"E14"),sQuery(id+"F0.wireOp",EDGE,"E15"),sQuery(id+"F0.wireOp",EDGE,"E16"),sQuery(id+"F0.wireOp",EDGE,"E20"),sQuery(id+"F0.wireOp",EDGE,"E22"),sQuery(id+"F0.wireOp",EDGE,"E23.MirrorCS"),sQuery(id+"F0.wireOp",EDGE,"E25.MirrorCS"),sQuery(id+"F0.wireOp",EDGE,"E26"),sQuery(id+"F0.wireOp",EDGE,"E27"),sQuery(id+"F0.wireOp",EDGE,"E30"),sQuery(id+"F0.wireOp",EDGE,"E32"),sQuery(id+"F0.wireOp",EDGE,"E33")])],"isStart":false})]});}
            var Q15;
            Q15=makeQuery(id+"F1.opExtrude","SWEPT_EDGE",EDGE,{"disambiguationData":[OSD([sQuery(id+"F0.wireOp",EDGE,"E18"),sQuery(id+"F0.wireOp",EDGE,"E22"),sQuery(id+"F0.wireOp",EDGE,"E33")])]});
            fillet(context, id + "F10", {"entities" : qUnion([Q0, Q1, Q2, Q3, Q4, Q5, Q6, Q7, Q8, Q9, Q10, Q11, Q12, Q13, Q14, Q15]), "tangentPropagation" : true, "radius" : 1.5 * mm, "defaultsChanged" : false, "vertexSettings" : [], "allowEdgeOverflow" : false});
        }
        {
            var Q0;
            Q0=makeQuery(id+"F1.opExtrude","SWEPT_EDGE",EDGE,{"disambiguationData":[OSD([sQuery(id+"F0.wireOp",EDGE,"E15"),sQuery(id+"F0.wireOp",EDGE,"E25.MirrorCS"),sQuery(id+"F0.wireOp",EDGE,"E31")])]});
            var Q1;
            Q1=makeQuery(id+"F1.opExtrude","CAP_EDGE",EDGE,{"disambiguationData":[OSD([sQuery(id+"F0.wireOp",EDGE,"E22")])],"isStart":false});
            fillet(context, id + "F11", {"entities" : qUnion([Q0, Q1]), "tangentPropagation" : true, "radius" : 2 * mm, "defaultsChanged" : false, "vertexSettings" : [], "allowEdgeOverflow" : false});
        }
        {
            var Q0;
            Q0=makeQuery(id+"F1.opExtrude","CAP_EDGE",EDGE,{"disambiguationData":[OSD([sQuery(id+"F0.wireOp",EDGE,"E15")])],"isStart":true});
            fillet(context, id + "F12", {"entities" : qUnion([Q0]), "tangentPropagation" : true, "radius" : .25 * mm, "defaultsChanged" : true, "vertexSettings" : [], "allowEdgeOverflow" : false});
        }
        {
            var Q0;
            Q0=makeQuery(id+"F1.opExtrude","SWEPT_EDGE",EDGE,{"disambiguationData":[OSD([sQuery(id+"F0.wireOp",EDGE,"E27"),sQuery(id+"F0.wireOp",EDGE,"E28.trimOffspring"),sQuery(id+"F0.wireOp",EDGE,"E30")])]});
            var Q1;
            Q1=makeQuery(id+"F1.opExtrude","SWEPT_EDGE",EDGE,{"disambiguationData":[OSD([sQuery(id+"F0.wireOp",EDGE,"E4"),sQuery(id+"F0.wireOp",EDGE,"E27")])]});
            var Q2;
            Q2=makeQuery(id+"F1.opExtrude","SWEPT_EDGE",EDGE,{"disambiguationData":[OSD([sQuery(id+"F0.wireOp",EDGE,"E4"),sQuery(id+"F0.wireOp",EDGE,"E26")])]});
            var Q3;
            Q3=makeQuery(id+"F1.opExtrude","SWEPT_EDGE",EDGE,{"disambiguationData":[OSD([sQuery(id+"F0.wireOp",EDGE,"E26"),sQuery(id+"F0.wireOp",EDGE,"E28.trimOffspring"),sQuery(id+"F0.wireOp",EDGE,"E30")])]});
            fillet(context, id + "F13", {"entities" : qUnion([Q0, Q1, Q2, Q3]), "tangentPropagation" : true, "radius" : 3 * mm, "defaultsChanged" : true, "vertexSettings" : [], "allowEdgeOverflow" : false});
        }
        {
            var Q0;
            Q0=makeQuery(id+"F1.opExtrude","CAP_EDGE",EDGE,{"disambiguationData":[OSD([sQuery(id+"F0.wireOp",EDGE,"E27")])],"isStart":false});
            fillet(context, id + "F14", {"entities" : qUnion([Q0]), "tangentPropagation" : true, "radius" : 1.5 * mm, "defaultsChanged" : false, "vertexSettings" : [], "allowEdgeOverflow" : false});
        }
        {
            var Q0;
            Q0=makeQuery(id+"F1.opExtrude","CAP_EDGE",EDGE,{"disambiguationData":[OSD([sQuery(id+"F0.wireOp",EDGE,"E27")])],"isStart":true});
            fillet(context, id + "F15", {"entities" : qUnion([Q0]), "tangentPropagation" : true, "radius" : .25 * mm, "defaultsChanged" : true, "vertexSettings" : [], "allowEdgeOverflow" : false});
        }
        {
            var Q0;
            {var subQ0=sQuery(id+"F0.wireOp",EDGE,"E4");var subQ7=makeQuery(id+"F0.imprint","INTERSECT",VERTEX,{"derivedFrom":[subQ0,sQuery(id+"F0.wireOp",EDGE,"E16")]});Q0=makeQuery(id+"F0.imprint","IMPRINT",FACE,{"disambiguationData":[TD([[makeQuery(id+"F0.imprint","IMPRINT",EDGE,{"disambiguationData":[TD([[subQ7,1.0]])],"derivedFrom":subQ0}),1.0]])]});}
            var Q1;
            {var subQ1=sQuery(id+"F0.wireOp",EDGE,"E4");var subQ6=makeQuery(id+"F0.imprint","INTERSECT",VERTEX,{"derivedFrom":[subQ1,sQuery(id+"F0.wireOp",EDGE,"E27")]});Q1=makeQuery(id+"F0.imprint","IMPRINT",FACE,{"disambiguationData":[TD([[makeQuery(id+"F0.imprint","IMPRINT",EDGE,{"disambiguationData":[TD([[subQ6,1.0]])],"derivedFrom":subQ1}),1.0]])]});}
            extrude(context, id + "F16", {"entities" : qUnion([Q0, Q1]), "depth" : 45 * mm, "offsetDistance" : 25 * mm, "hasSecondDirection" : true, "secondDirectionOppositeDirection" : false, "secondDirectionDepth" : 5 * mm});
        }
        {
            var Q0;
            Q0=makeQuery(id+"F16.opExtrude","CAP_FACE",FACE,{"disambiguationData":[OSD([sQuery(id+"F0.wireOp",EDGE,"E4"),sQuery(id+"F0.wireOp",EDGE,"E10")])],"isStart":false});
            var sketch = newSketch(context, id + "F17", { "sketchPlane" : qUnion([Q0])});
            skCircle(sketch, "E34.0", {"center": v(0, -54.9) * mm, "radius": 15.9 * mm});
            skSolve(sketch);
        }
        {
            var Q0;
            Q0 = qSketchRegion(id + "F17", true);
            extrude(context, id + "F18", {"entities" : qUnion([Q0]), "operationType" : NewBodyOperationType.ADD, "oppositeDirection" : true, "depth" : 5 * mm, "offsetDistance" : 25 * mm});
        }
        {
            var Q0;
            Q0=makeQuery(id+"F16.opExtrude","CAP_EDGE",EDGE,{"disambiguationData":[OSD([sQuery(id+"F0.wireOp",EDGE,"E4")])],"isStart":false});
            fillet(context, id + "F19", {"entities" : qUnion([Q0]), "tangentPropagation" : true, "radius" : 3 * mm, "defaultsChanged" : true, "vertexSettings" : [], "allowEdgeOverflow" : false});
        }
        {
            var Q0;
            Q0=makeQuery(id+"F18.boolean.opBoolean","MERGE",FACE,{"derivedFrom":[makeQuery(id+"F16.opExtrude","CAP_FACE",FACE,{"disambiguationData":[OSD([sQuery(id+"F0.wireOp",EDGE,"E4"),sQuery(id+"F0.wireOp",EDGE,"E10")])],"isStart":false}),makeQuery(id+"F18.opExtrude","CAP_FACE",FACE,{"disambiguationData":[OSD([sQuery(id+"F17.wireOp",EDGE,"E34.0")])],"isStart":true})]});
            var sketch = newSketch(context, id + "F20", { "sketchPlane" : qUnion([Q0])});
            skCircle(sketch, "E35", {"center": v(0, -54.9) * mm, "radius": 3.25 * mm});
            skCircle(sketch, "E36", {"center": v(0, -54.9) * mm, "radius": 5 * mm});
            skSolve(sketch);
        }
        {
            var Q0;
            Q0=makeQuery(id+"F20.imprint","IMPRINT",FACE,{"disambiguationData":[TD([[makeQuery(id+"F20.imprint","IMPRINT",EDGE,{"derivedFrom":sQuery(id+"F20.wireOp",EDGE,"E35")}),-1.0]])]});
            var Q1;
            Q1=makeQuery(id+"F20.imprint","IMPRINT",FACE,{"disambiguationData":[TD([[makeQuery(id+"F20.imprint","IMPRINT",EDGE,{"derivedFrom":sQuery(id+"F20.wireOp",EDGE,"E35")}),1.0]])]});
            extrude(context, id + "F21", {"entities" : qUnion([Q0, Q1]), "operationType" : NewBodyOperationType.REMOVE, "oppositeDirection" : true, "depth" : 3 * mm, "offsetDistance" : 25 * mm});
        }
        {
            var Q0;
            Q0=makeQuery(id+"F20.imprint","IMPRINT",FACE,{"disambiguationData":[TD([[makeQuery(id+"F20.imprint","IMPRINT",EDGE,{"derivedFrom":sQuery(id+"F20.wireOp",EDGE,"E35")}),1.0]])]});
            var Q1;
            Q1=sQuery(id+"F20.wireOp",EDGE,"E35");
            extrude(context, id + "F22", {"entities" : qUnion([Q0]), "operationType" : NewBodyOperationType.REMOVE, "surfaceEntities" : qUnion([Q1]), "oppositeDirection" : true, "depth" : 25 * mm, "offsetDistance" : 25 * mm});
        }
    });
